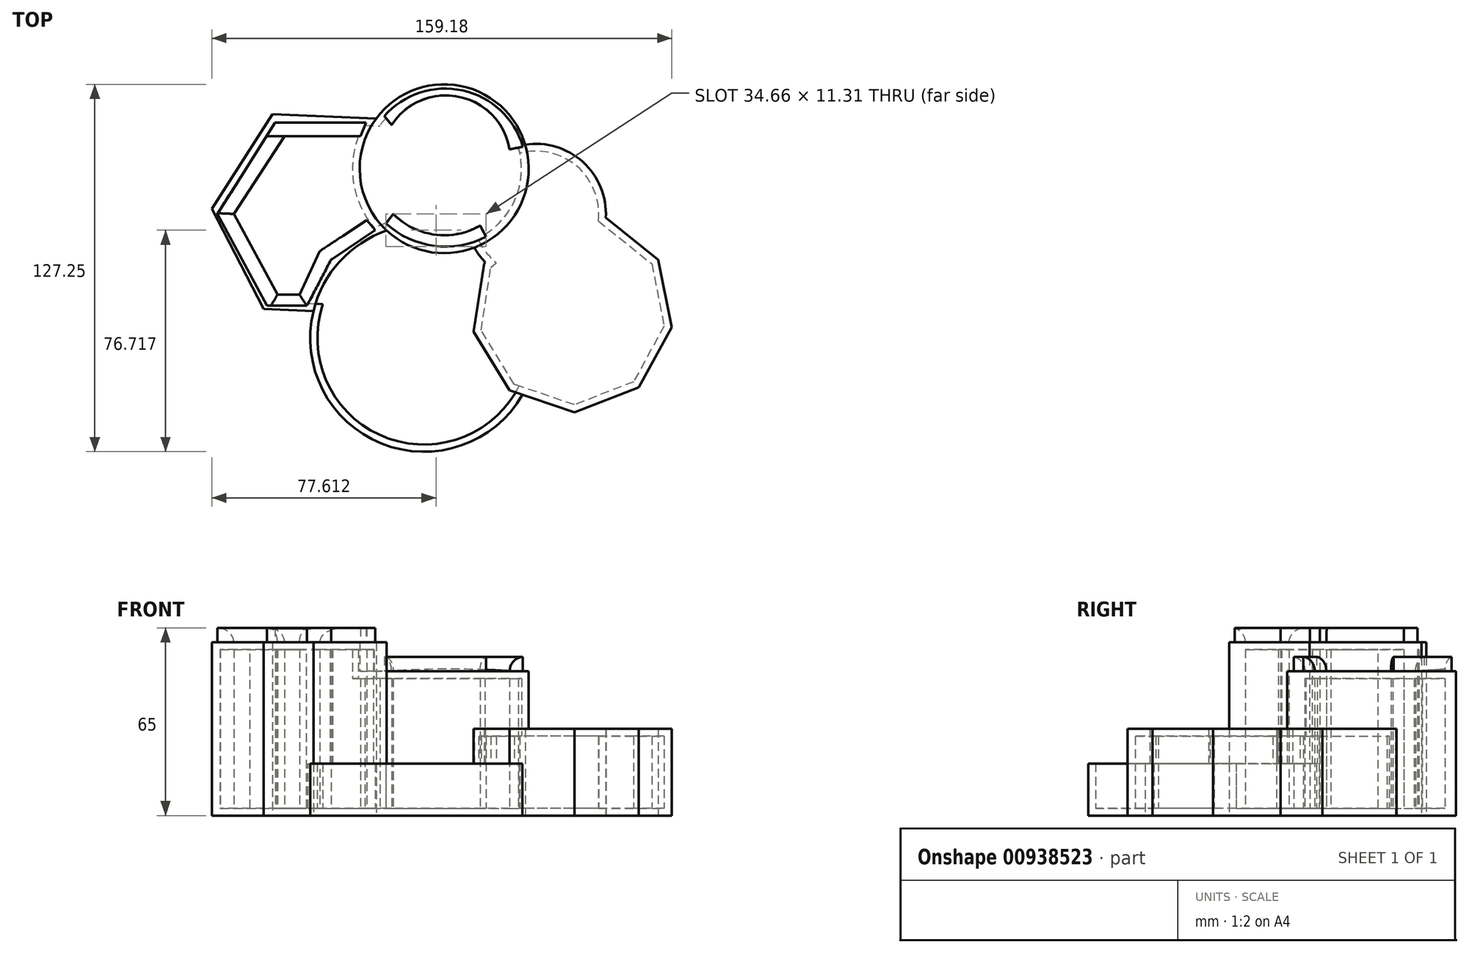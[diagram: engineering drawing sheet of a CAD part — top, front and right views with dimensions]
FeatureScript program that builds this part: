
annotation { "Feature Type Name" : "Feature", "Feature Type Description" : "" }
export const myFeature = defineFeature(function(context is Context, id is Id, definition is map)
    precondition{}
    {
        {
            var Q0;
            Q0=qCreatedBy(makeId("Top.planeOp"),FACE);
            var sketch = newSketch(context, id + "F0", { "sketchPlane" : qUnion([Q0])});
            skCircle(sketch, "E0", {"center": v(-25.27, 15.64) * mm, "radius": 29.24 * mm});
            skCircle(sketch, "E1", {"center": v(6.45, 0) * mm, "radius": 24.26 * mm});
            skCircle(sketch, "E2", {"center": v(-32.27, -42.98) * mm, "radius": 39.4 * mm});
            skCircle(sketch, "E3.cCircle", {"center": v(-66.77, 0) * mm, "radius": 33.75 * mm, "construction": true});
            skLineSegment(sketch, "E3.0", {"start": v(-27.84, -1.72) * mm, "end": v(-48.79, -34.58) * mm});
            skLineSegment(sketch, "E3.1", {"start": v(-48.79, -34.58) * mm, "end": v(-87.72, -32.86) * mm});
            skLineSegment(sketch, "E3.2", {"start": v(-87.72, -32.86) * mm, "end": v(-105.7, 1.72) * mm});
            skLineSegment(sketch, "E3.3", {"start": v(-105.7, 1.72) * mm, "end": v(-84.75, 34.58) * mm});
            skLineSegment(sketch, "E3.4", {"start": v(-84.75, 34.58) * mm, "end": v(-45.82, 32.86) * mm});
            skLineSegment(sketch, "E3.5", {"start": v(-45.82, 32.86) * mm, "end": v(-27.84, -1.72) * mm});
            skPoint(sketch, "E3.0.midPoint", {"position": v(-38.31, -18.15) * mm});
            skCircle(sketch, "E4.cCircle", {"center": v(19.08, -33.95) * mm, "radius": 32.71 * mm, "construction": true});
            skLineSegment(sketch, "E4.0", {"start": v(53.48, -39.25) * mm, "end": v(42.03, -60.13) * mm});
            skLineSegment(sketch, "E4.1", {"start": v(42.03, -60.13) * mm, "end": v(19.84, -68.76) * mm});
            skLineSegment(sketch, "E4.2", {"start": v(19.84, -68.76) * mm, "end": v(-2.71, -61.1) * mm});
            skLineSegment(sketch, "E4.3", {"start": v(-2.71, -61.1) * mm, "end": v(-15.06, -40.75) * mm});
            skLineSegment(sketch, "E4.4", {"start": v(-15.06, -40.75) * mm, "end": v(-11.44, -17.21) * mm});
            skLineSegment(sketch, "E4.5", {"start": v(-11.44, -17.21) * mm, "end": v(6.46, -1.51) * mm});
            skLineSegment(sketch, "E4.6", {"start": v(6.46, -1.51) * mm, "end": v(30.27, -1) * mm});
            skLineSegment(sketch, "E4.7", {"start": v(30.27, -1) * mm, "end": v(48.84, -15.9) * mm});
            skLineSegment(sketch, "E4.8", {"start": v(48.84, -15.9) * mm, "end": v(53.48, -39.25) * mm});
            skPoint(sketch, "E4.0.midPoint", {"position": v(47.76, -49.69) * mm});
            skSolve(sketch);
        }
        {
            var Q0;
            {var subQ0=sQuery(id+"F0.wireOp",EDGE,"E2");var subQ1=sQuery(id+"F0.wireOp",EDGE,"E0");var subQ2=makeQuery(id+"F0.imprint","INTERSECT",VERTEX,{"disambiguationData":[OD(0.0)],"derivedFrom":[subQ1,subQ0]});Q0=makeQuery(id+"F0.imprint","IMPRINT",FACE,{"disambiguationData":[TD([[makeQuery(id+"F0.imprint","IMPRINT",EDGE,{"disambiguationData":[TD([[subQ2,1.0]])],"derivedFrom":subQ1}),1.0]])]});}
            var Q1;
            {var subQ5=sQuery(id+"F0.wireOp",EDGE,"E3.5");Q1=makeQuery(id+"F0.imprint","IMPRINT",FACE,{"disambiguationData":[TD([[makeQuery(id+"F0.imprint","IMPRINT",EDGE,{"derivedFrom":subQ5}),1.0]])]});}
            var Q2;
            {var subQ0=sQuery(id+"F0.wireOp",EDGE,"E1");var subQ1=sQuery(id+"F0.wireOp",EDGE,"E0");var subQ2=makeQuery(id+"F0.imprint","INTERSECT",VERTEX,{"disambiguationData":[OD(0.0)],"derivedFrom":[subQ1,subQ0]});Q2=makeQuery(id+"F0.imprint","IMPRINT",FACE,{"disambiguationData":[TD([[makeQuery(id+"F0.imprint","IMPRINT",EDGE,{"disambiguationData":[TD([[subQ2,1.0]])],"derivedFrom":subQ1}),1.0]])]});}
            var Q3;
            {var subQ0=sQuery(id+"F0.wireOp",EDGE,"E2");var subQ1=sQuery(id+"F0.wireOp",EDGE,"E0");var subQ2=makeQuery(id+"F0.imprint","INTERSECT",VERTEX,{"disambiguationData":[OD(0.0)],"derivedFrom":[subQ1,subQ0]});Q3=makeQuery(id+"F0.imprint","IMPRINT",FACE,{"disambiguationData":[TD([[makeQuery(id+"F0.imprint","IMPRINT",EDGE,{"disambiguationData":[TD([[subQ2,-1.0]])],"derivedFrom":subQ1}),1.0]])]});}
            var Q4;
            {var subQ0=sQuery(id+"F0.wireOp",EDGE,"E1");var subQ1=sQuery(id+"F0.wireOp",EDGE,"E0");var subQ2=makeQuery(id+"F0.imprint","INTERSECT",VERTEX,{"disambiguationData":[OD(1.0)],"derivedFrom":[subQ1,subQ0]});Q4=makeQuery(id+"F0.imprint","IMPRINT",FACE,{"disambiguationData":[TD([[makeQuery(id+"F0.imprint","IMPRINT",EDGE,{"disambiguationData":[TD([[subQ2,-1.0]])],"derivedFrom":subQ1}),1.0]])]});}
            var Q5;
            {var subQ0=sQuery(id+"F0.wireOp",EDGE,"E3.0");var subQ1=sQuery(id+"F0.wireOp",EDGE,"E0");var subQ2=makeQuery(id+"F0.imprint","INTERSECT",VERTEX,{"derivedFrom":[subQ1,subQ0]});Q5=makeQuery(id+"F0.imprint","IMPRINT",FACE,{"disambiguationData":[TD([[makeQuery(id+"F0.imprint","IMPRINT",EDGE,{"disambiguationData":[TD([[subQ2,-1.0]])],"derivedFrom":subQ1}),1.0]])]});}
            extrude(context, id + "F1", {"entities" : qUnion([Q0, Q1, Q2, Q3, Q4, Q5]), "depth" : 50 * mm, "offsetDistance" : 25 * mm});
        }
        {
            var Q0;
            {var subQ0=sQuery(id+"F0.wireOp",EDGE,"E1");var subQ1=sQuery(id+"F0.wireOp",EDGE,"E0");var subQ2=makeQuery(id+"F0.imprint","INTERSECT",VERTEX,{"disambiguationData":[OD(0.0)],"derivedFrom":[subQ1,subQ0]});Q0=makeQuery(id+"F0.imprint","IMPRINT",FACE,{"disambiguationData":[TD([[makeQuery(id+"F0.imprint","IMPRINT",EDGE,{"disambiguationData":[TD([[subQ2,1.0]])],"derivedFrom":subQ1}),1.0]])]});}
            var Q1;
            {var subQ0=sQuery(id+"F0.wireOp",EDGE,"E2");var subQ1=sQuery(id+"F0.wireOp",EDGE,"E0");var subQ2=makeQuery(id+"F0.imprint","INTERSECT",VERTEX,{"disambiguationData":[OD(0.0)],"derivedFrom":[subQ1,subQ0]});Q1=makeQuery(id+"F0.imprint","IMPRINT",FACE,{"disambiguationData":[TD([[makeQuery(id+"F0.imprint","IMPRINT",EDGE,{"disambiguationData":[TD([[subQ2,-1.0]])],"derivedFrom":subQ1}),1.0]])]});}
            var Q2;
            {var subQ0=sQuery(id+"F0.wireOp",EDGE,"E1");var subQ1=sQuery(id+"F0.wireOp",EDGE,"E0");var subQ2=makeQuery(id+"F0.imprint","INTERSECT",VERTEX,{"disambiguationData":[OD(1.0)],"derivedFrom":[subQ1,subQ0]});Q2=makeQuery(id+"F0.imprint","IMPRINT",FACE,{"disambiguationData":[TD([[makeQuery(id+"F0.imprint","IMPRINT",EDGE,{"disambiguationData":[TD([[subQ2,-1.0]])],"derivedFrom":subQ1}),1.0]])]});}
            extrude(context, id + "F2", {"entities" : qUnion([Q0, Q1, Q2]), "operationType" : NewBodyOperationType.ADD, "depth" : 50 * mm, "offsetDistance" : 25 * mm});
        }
        {
            var Q0;
            {var subQ0=sQuery(id+"F0.wireOp",EDGE,"E1");var subQ1=sQuery(id+"F0.wireOp",EDGE,"E0");var subQ2=makeQuery(id+"F0.imprint","INTERSECT",VERTEX,{"disambiguationData":[OD(0.0)],"derivedFrom":[subQ1,subQ0]});Q0=makeQuery(id+"F0.imprint","IMPRINT",FACE,{"disambiguationData":[TD([[makeQuery(id+"F0.imprint","IMPRINT",EDGE,{"disambiguationData":[TD([[subQ2,1.0]])],"derivedFrom":subQ1}),-1.0]])]});}
            var Q1;
            {var subQ0=sQuery(id+"F0.wireOp",EDGE,"E1");var subQ1=sQuery(id+"F0.wireOp",EDGE,"E0");var subQ2=makeQuery(id+"F0.imprint","INTERSECT",VERTEX,{"disambiguationData":[OD(1.0)],"derivedFrom":[subQ1,subQ0]});Q1=makeQuery(id+"F0.imprint","IMPRINT",FACE,{"disambiguationData":[TD([[makeQuery(id+"F0.imprint","IMPRINT",EDGE,{"disambiguationData":[TD([[subQ2,-1.0]])],"derivedFrom":subQ1}),-1.0]])]});}
            var Q2;
            {var subQ0=sQuery(id+"F0.wireOp",EDGE,"E4.6");Q2=makeQuery(id+"F0.imprint","IMPRINT",FACE,{"disambiguationData":[TD([[makeQuery(id+"F0.imprint","IMPRINT",EDGE,{"derivedFrom":subQ0}),-1.0]])]});}
            var Q3;
            {var subQ0=sQuery(id+"F0.wireOp",EDGE,"E4.5");var subQ1=sQuery(id+"F0.wireOp",EDGE,"E1");var subQ2=makeQuery(id+"F0.imprint","INTERSECT",VERTEX,{"derivedFrom":[subQ1,subQ0]});Q3=makeQuery(id+"F0.imprint","IMPRINT",FACE,{"disambiguationData":[TD([[makeQuery(id+"F0.imprint","IMPRINT",EDGE,{"disambiguationData":[TD([[subQ2,-1.0]])],"derivedFrom":subQ1}),1.0]])]});}
            var Q4;
            {var subQ0=sQuery(id+"F0.wireOp",EDGE,"E4.3");Q4=makeQuery(id+"F0.imprint","IMPRINT",FACE,{"disambiguationData":[TD([[makeQuery(id+"F0.imprint","IMPRINT",EDGE,{"derivedFrom":subQ0}),-1.0]])]});}
            var Q5;
            Q5=makeQuery(id+"F0.imprint","IMPRINT",FACE,{"disambiguationData":[TD([[makeQuery(id+"F0.imprint","IMPRINT",EDGE,{"derivedFrom":sQuery(id+"F0.wireOp",EDGE,"E4.0")}),-1.0]])]});
            extrude(context, id + "F3", {"entities" : qUnion([Q0, Q1, Q2, Q3, Q4, Q5]), "operationType" : NewBodyOperationType.ADD, "depth" : 30 * mm, "offsetDistance" : 25 * mm});
        }
        {
            var Q0;
            {var subQ0=sQuery(id+"F0.wireOp",EDGE,"E2");var subQ1=sQuery(id+"F0.wireOp",EDGE,"E0");var subQ2=makeQuery(id+"F0.imprint","INTERSECT",VERTEX,{"disambiguationData":[OD(0.0)],"derivedFrom":[subQ1,subQ0]});Q0=makeQuery(id+"F0.imprint","IMPRINT",FACE,{"disambiguationData":[TD([[makeQuery(id+"F0.imprint","IMPRINT",EDGE,{"disambiguationData":[TD([[subQ2,-1.0]])],"derivedFrom":subQ1}),-1.0]])]});}
            var Q1;
            {var subQ5=sQuery(id+"F0.wireOp",EDGE,"E4.3");Q1=makeQuery(id+"F0.imprint","IMPRINT",FACE,{"disambiguationData":[TD([[makeQuery(id+"F0.imprint","IMPRINT",EDGE,{"derivedFrom":subQ5}),1.0]])]});}
            extrude(context, id + "F4", {"entities" : qUnion([Q0, Q1]), "operationType" : NewBodyOperationType.ADD, "depth" : 18 * mm, "offsetDistance" : 25 * mm});
        }
        {
            var Q0;
            {var subQ0=sQuery(id+"F0.wireOp",EDGE,"E3.2");Q0=makeQuery(id+"F0.imprint","IMPRINT",FACE,{"disambiguationData":[TD([[makeQuery(id+"F0.imprint","IMPRINT",EDGE,{"derivedFrom":subQ0}),-1.0]])]});}
            extrude(context, id + "F5", {"entities" : qUnion([Q0]), "operationType" : NewBodyOperationType.ADD, "depth" : 60 * mm, "offsetDistance" : 25 * mm});
        }
        {
            var Q0;
            Q0=makeQuery(id+"F4.opExtrude","CAP_FACE",FACE,{"disambiguationData":[OSD([sQuery(id+"F0.wireOp",EDGE,"E0"),sQuery(id+"F0.wireOp",EDGE,"E1"),sQuery(id+"F0.wireOp",EDGE,"E2"),sQuery(id+"F0.wireOp",EDGE,"E4.2"),sQuery(id+"F0.wireOp",EDGE,"E4.3"),sQuery(id+"F0.wireOp",EDGE,"E4.4"),sQuery(id+"F0.wireOp",EDGE,"E4.5")])],"isStart":false});
            shell(context, id + "F6", {"entities" : qUnion([Q0]), "thickness" : 2.5 * mm});
        }
        {
            var Q0;
            Q0=qCreatedBy(makeId("Top.planeOp"),FACE);
            var sketch = newSketch(context, id + "F7", { "sketchPlane" : qUnion([Q0])});
            skLineSegment(sketch, "E5", {"start": v(-49.17, -5.62) * mm, "end": v(-64.4, -15.8) * mm});
            skLineSegment(sketch, "E6", {"start": v(-64.4, -15.8) * mm, "end": v(-72.7, -31.7) * mm});
            skLineSegment(sketch, "E7", {"start": v(-72.7, -31.7) * mm, "end": v(-86.59, -31.7) * mm});
            skLineSegment(sketch, "E8", {"start": v(-86.59, -31.7) * mm, "end": v(-103.73, 0) * mm});
            skLineSegment(sketch, "E9", {"start": v(-103.73, 0) * mm, "end": v(-83.8, 31.55) * mm});
            skLineSegment(sketch, "E10", {"start": v(-83.8, 31.55) * mm, "end": v(-52.3, 31.55) * mm});
            skLineSegment(sketch, "E11", {"start": v(-52.3, 31.55) * mm, "end": v(-54.27, 26.89) * mm});
            skLineSegment(sketch, "E12", {"start": v(-54.27, 26.89) * mm, "end": v(-80.49, 26.89) * mm});
            skLineSegment(sketch, "E13", {"start": v(-80.49, 26.89) * mm, "end": v(-98.06, 0) * mm});
            skLineSegment(sketch, "E14", {"start": v(-98.06, 0) * mm, "end": v(-82.94, -27.97) * mm});
            skLineSegment(sketch, "E15", {"start": v(-82.94, -27.97) * mm, "end": v(-75.32, -27.97) * mm});
            skLineSegment(sketch, "E16", {"start": v(-75.32, -27.97) * mm, "end": v(-68.29, -12.85) * mm});
            skLineSegment(sketch, "E17", {"start": v(-68.29, -12.85) * mm, "end": v(-52.08, -2.18) * mm});
            skLineSegment(sketch, "E18", {"start": v(-52.08, -2.18) * mm, "end": v(-49.17, -5.62) * mm});
            skArc(sketch, "E19", {"start": v(-45.42, -3.34) * mm, "mid": v(-28.8, -11.05) * mm, "end": v(-10.76, -7.93) * mm});
            skArc(sketch, "E20", {"start": v(-42.9, 0) * mm, "mid": v(-28.55, -7.17) * mm, "end": v(-12.83, -4.03) * mm});
            skLineSegment(sketch, "E21", {"start": v(-12.83, -4.03) * mm, "end": v(-10.76, -7.93) * mm});
            skLineSegment(sketch, "E22", {"start": v(-42.9, 0) * mm, "end": v(-45.42, -3.34) * mm});
            skArc(sketch, "E23", {"start": v(1.98, 23.28) * mm, "mid": v(-18.88, 42.74) * mm, "end": v(-45.99, 33.84) * mm});
            skArc(sketch, "E24", {"start": v(-2.61, 22.36) * mm, "mid": v(-20.14, 40.58) * mm, "end": v(-43.47, 30.85) * mm});
            skLineSegment(sketch, "E25", {"start": v(-45.99, 33.84) * mm, "end": v(-43.47, 30.85) * mm});
            skLineSegment(sketch, "E26", {"start": v(1.98, 23.28) * mm, "end": v(-2.61, 22.36) * mm});
            skSolve(sketch);
        }
        {
            var Q0;
            Q0=makeQuery(id+"F7.imprint","IMPRINT",FACE,{"disambiguationData":[TD([[makeQuery(id+"F7.imprint","IMPRINT",EDGE,{"derivedFrom":sQuery(id+"F7.wireOp",EDGE,"E5")}),-1.0]])]});
            extrude(context, id + "F8", {"entities" : qUnion([Q0]), "operationType" : NewBodyOperationType.ADD, "depth" : 65 * mm, "offsetDistance" : 25 * mm});
        }
        {
            var Q0;
            Q0=makeQuery(id+"F8.opExtrude","CAP_EDGE",EDGE,{"disambiguationData":[OSD([sQuery(id+"F7.wireOp",EDGE,"E13")])],"isStart":false});
            var Q1;
            Q1=makeQuery(id+"F8.opExtrude","CAP_EDGE",EDGE,{"disambiguationData":[OSD([sQuery(id+"F7.wireOp",EDGE,"E14")])],"isStart":false});
            var Q2;
            Q2=makeQuery(id+"F8.opExtrude","CAP_EDGE",EDGE,{"disambiguationData":[OSD([sQuery(id+"F7.wireOp",EDGE,"E15")])],"isStart":false});
            var Q3;
            Q3=makeQuery(id+"F8.opExtrude","CAP_EDGE",EDGE,{"disambiguationData":[OSD([sQuery(id+"F7.wireOp",EDGE,"E16")])],"isStart":false});
            fillet(context, id + "F9", {"entities" : qUnion([Q0, Q1, Q2, Q3]), "radius" : 5 * mm, "tangentPropagation" : true, "allowEdgeOverflow" : false});
        }
        {
            var Q0;
            Q0=makeQuery(id+"F7.imprint","IMPRINT",FACE,{"disambiguationData":[TD([[makeQuery(id+"F7.imprint","IMPRINT",EDGE,{"derivedFrom":sQuery(id+"F7.wireOp",EDGE,"E23")}),1.0]])]});
            var Q1;
            Q1=makeQuery(id+"F7.imprint","IMPRINT",FACE,{"disambiguationData":[TD([[makeQuery(id+"F7.imprint","IMPRINT",EDGE,{"derivedFrom":sQuery(id+"F7.wireOp",EDGE,"E19")}),1.0]])]});
            extrude(context, id + "F10", {"entities" : qUnion([Q0, Q1]), "operationType" : NewBodyOperationType.ADD, "depth" : 55 * mm, "offsetDistance" : 25 * mm});
        }
        {
            var Q0;
            Q0=makeQuery(id+"F10.opExtrude","CAP_EDGE",EDGE,{"disambiguationData":[OSD([sQuery(id+"F7.wireOp",EDGE,"E24")])],"isStart":false});
            var Q1;
            Q1=makeQuery(id+"F10.opExtrude","CAP_EDGE",EDGE,{"disambiguationData":[OSD([sQuery(id+"F7.wireOp",EDGE,"E20")])],"isStart":false});
            fillet(context, id + "F11", {"entities" : qUnion([Q0, Q1]), "radius" : 5 * mm, "tangentPropagation" : true, "allowEdgeOverflow" : false});
        }
    });
